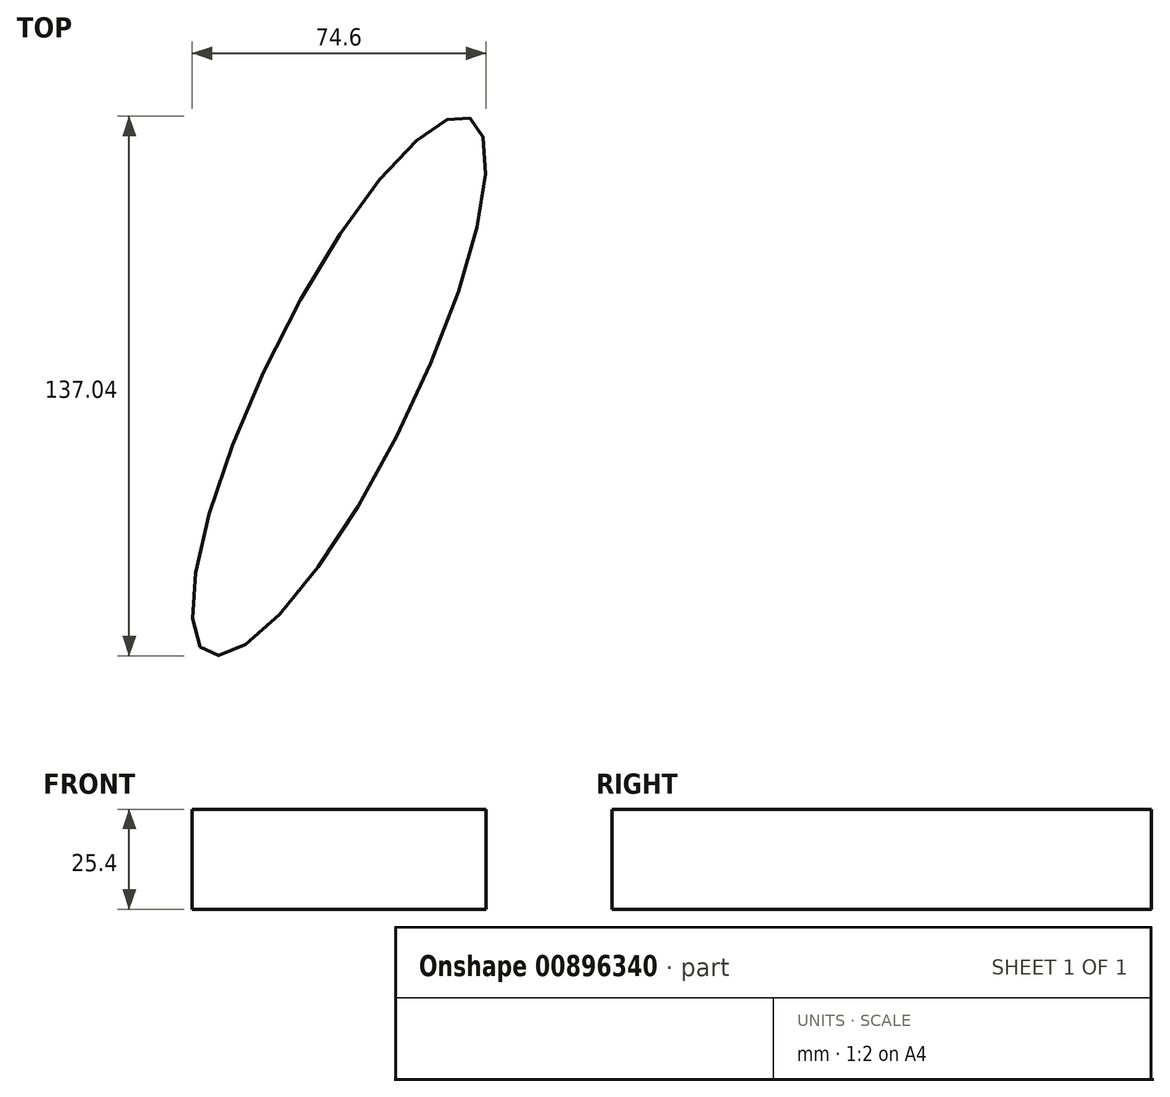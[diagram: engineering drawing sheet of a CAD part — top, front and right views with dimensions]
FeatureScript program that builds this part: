
annotation { "Feature Type Name" : "Feature", "Feature Type Description" : "" }
export const myFeature = defineFeature(function(context is Context, id is Id, definition is map)
    precondition{}
    {
        {
            var Q0;
            Q0=qCreatedBy(makeId("Top.planeOp"),FACE);
            var sketch = newSketch(context, id + "F0", { "sketchPlane" : qUnion([Q0])});
            skEllipse(sketch, "E0", {"center": v(0, 0) * mm, "majorRadius": 75.72 * mm, "minorRadius": 18.8 * mm, "majorAxis": v(0.44, 0.9)});
            skSolve(sketch);
        }
        {
            var Q0;
            Q0 = qSketchRegion(id + "F0", true);
            extrude(context, id + "F1", {"entities" : qUnion([Q0]), "depth" : 25.4 * mm, "offsetDistance" : 25.4 * mm});
        }
    });
